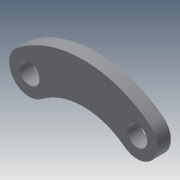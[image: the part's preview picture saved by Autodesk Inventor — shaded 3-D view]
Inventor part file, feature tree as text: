
AUTODESK INVENTOR PART (.ipt)
format: ipt  version: 2013 (Build 170138000, 138)  size: 89,600 bytes
history: native  units: mm
features: extrude x1, sketch x1
ambient origin geometry x8: Origin, YZ Plane, XZ Plane, XY Plane, X Axis, Y Axis, Z Axis, Center Point
bodies: Solid1 (feature_tree)
feature tree (2):
  extrude  "Extrusion1"  Depth=6.0mm
  sketch  "Sketch1"  dims[d13=16.0mm d14=6.0mm d16=6.0mm d17=3.0mm d18=3.0mm d19=2.0mm d20=0.0mm]
